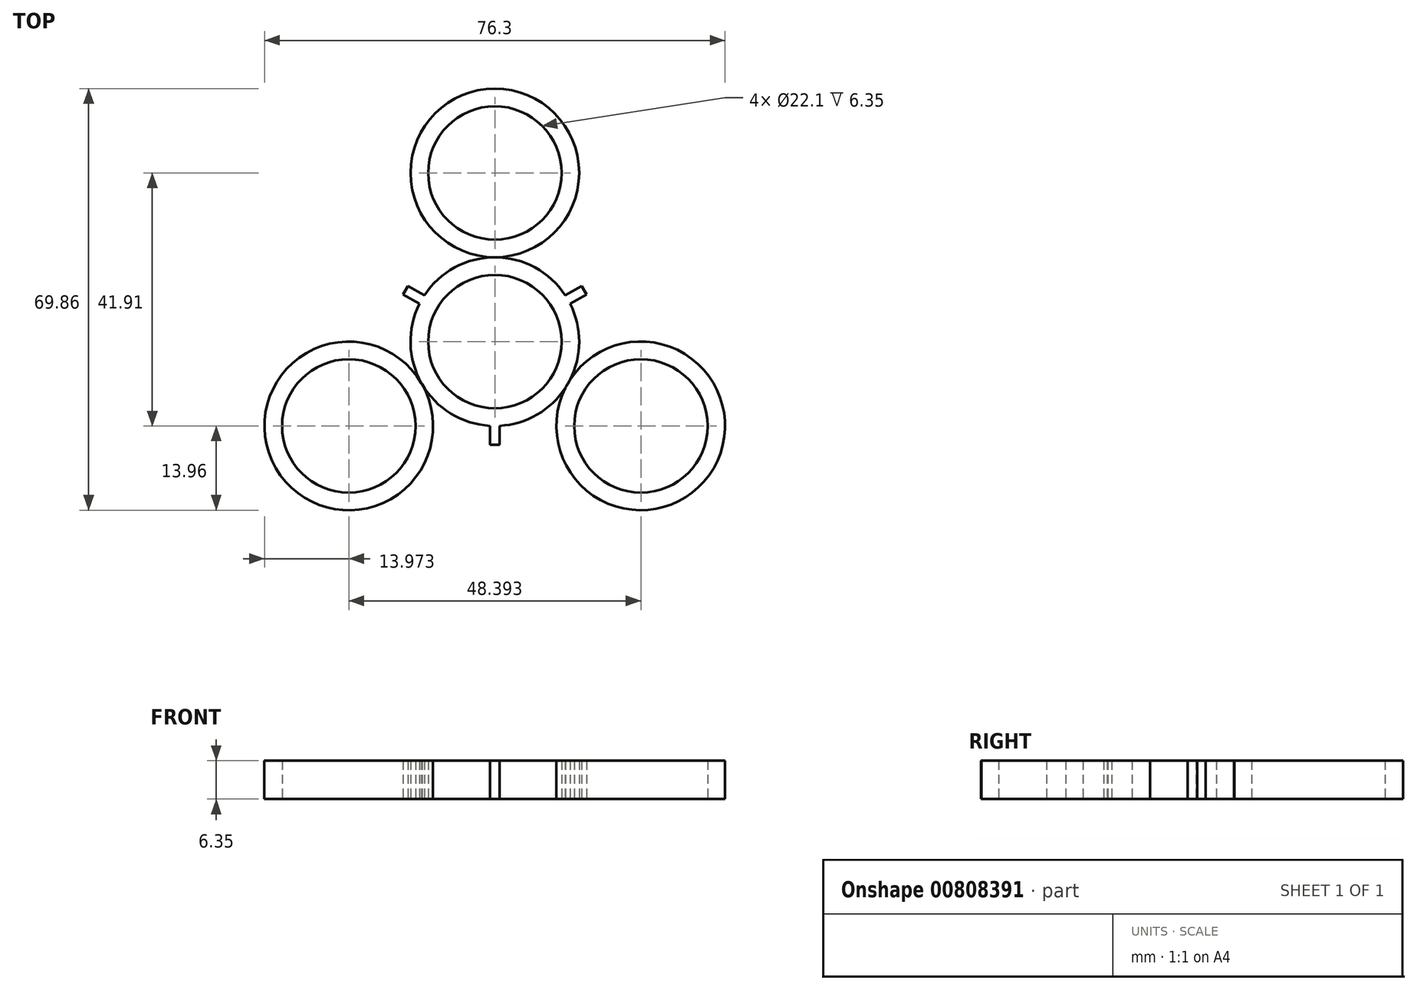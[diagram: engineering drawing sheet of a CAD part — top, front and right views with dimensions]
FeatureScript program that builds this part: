
annotation { "Feature Type Name" : "Feature", "Feature Type Description" : "" }
export const myFeature = defineFeature(function(context is Context, id is Id, definition is map)
    precondition{}
    {
        {
            var Q0;
            Q0=qCreatedBy(makeId("Top.planeOp"),FACE);
            var sketch = newSketch(context, id + "F0", { "sketchPlane" : qUnion([Q0])});
            skCircle(sketch, "E0", {"center": v(0, 0) * mm, "radius": 44.45 * mm});
            skCircle(sketch, "E1", {"center": v(0, 0) * mm, "radius": 11.05 * mm});
            skLineSegment(sketch, "E2", {"start": v(0, 0) * mm, "end": v(0, 27.94) * mm});
            skCircle(sketch, "E3", {"center": v(0, 27.94) * mm, "radius": 11.05 * mm});
            skCircle(sketch, "E4.1.0", {"center": v(-24.2, -13.97) * mm, "radius": 11.05 * mm});
            skCircle(sketch, "E4.2.0", {"center": v(24.2, -13.97) * mm, "radius": 11.05 * mm});
            skSolve(sketch);
        }
        {
            var Q0;
            Q0=makeQuery(id+"F0.imprint","IMPRINT",FACE,{"disambiguationData":[TD([[makeQuery(id+"F0.imprint","IMPRINT",EDGE,{"derivedFrom":sQuery(id+"F0.wireOp",EDGE,"E0")}),1.0]])]});
            var sketch = newSketch(context, id + "F1", { "sketchPlane" : qUnion([Q0])});
            skCircle(sketch, "E5", {"center": v(0, 27.96) * mm, "radius": 13.97 * mm});
            skCircle(sketch, "E6", {"center": v(24.16, -13.95) * mm, "radius": 13.97 * mm});
            skCircle(sketch, "E7", {"center": v(0, 0) * mm, "radius": 13.97 * mm});
            skCircle(sketch, "E8", {"center": v(-24.2, -13.96) * mm, "radius": 13.97 * mm});
            skSolve(sketch);
        }
        {
            var Q0;
            Q0=makeQuery(id+"F1.imprint","IMPRINT",FACE,{"disambiguationData":[TD([[makeQuery(id+"F1.imprint","IMPRINT",EDGE,{"derivedFrom":sQuery(id+"F1.wireOp",EDGE,"E5")}),1.0]])]});
            var Q1;
            Q1=makeQuery(id+"F1.imprint","IMPRINT",FACE,{"disambiguationData":[TD([[makeQuery(id+"F1.imprint","IMPRINT",EDGE,{"derivedFrom":makeQuery(id+"F0.imprint","IMPRINT",EDGE,{"derivedFrom":sQuery(id+"F0.wireOp",EDGE,"E1")})}),-1.0]])]});
            var Q2;
            Q2=makeQuery(id+"F1.imprint","IMPRINT",FACE,{"disambiguationData":[TD([[makeQuery(id+"F1.imprint","IMPRINT",EDGE,{"derivedFrom":makeQuery(id+"F0.imprint","IMPRINT",EDGE,{"derivedFrom":sQuery(id+"F0.wireOp",EDGE,"E4.1.0")})}),-1.0]])]});
            var Q3;
            Q3=makeQuery(id+"F1.imprint","IMPRINT",FACE,{"disambiguationData":[TD([[makeQuery(id+"F1.imprint","IMPRINT",EDGE,{"derivedFrom":makeQuery(id+"F0.imprint","IMPRINT",EDGE,{"derivedFrom":sQuery(id+"F0.wireOp",EDGE,"E4.2.0")})}),-1.0]])]});
            extrude(context, id + "F2", {"entities" : qUnion([Q0, Q1, Q2, Q3]), "depth" : 6.35 * mm, "offsetDistance" : 25.4 * mm});
        }
        {
            var Q0;
            Q0=qCreatedBy(makeId("Top.planeOp"),FACE);
            var sketch = newSketch(context, id + "F3", { "sketchPlane" : qUnion([Q0])});
            skArc(sketch, "E9", {"start": v(11.46, -19.74) * mm, "mid": v(-0.17, -17.05) * mm, "end": v(-11.76, -19.93) * mm});
            skArc(sketch, "E10.1.0", {"start": v(11.37, 19.8) * mm, "mid": v(14.85, 8.38) * mm, "end": v(23.14, -0.22) * mm});
            skArc(sketch, "E10.2.0", {"start": v(-22.83, -0.05) * mm, "mid": v(-14.68, 8.67) * mm, "end": v(-11.38, 20.15) * mm});
            skPoint(sketch, "E10.center", {"position": v(0, 0) * mm});
            skSolve(sketch);
        }
        {
            var Q0;
            Q0=sQuery(id+"F3.wireOp",EDGE,"E9");
            extrude(context, id + "F4", {"bodyType" : ToolBodyType.SURFACE, "surfaceEntities" : qUnion([Q0]), "depth" : 6.35 * mm, "offsetDistance" : 25.4 * mm});
        }
        {
            var Q0;
            Q0=sQuery(id+"F3.wireOp",EDGE,"E10.2.0");
            var Q1;
            Q1=sQuery(id+"F3.wireOp",EDGE,"E10.1.0");
            extrude(context, id + "F5", {"bodyType" : ToolBodyType.SURFACE, "surfaceEntities" : qUnion([Q0, Q1]), "depth" : 6.35 * mm, "offsetDistance" : 25.4 * mm});
        }
        {
            var Q0;
            Q0=qCreatedBy(makeId("Top.planeOp"),FACE);
            var sketch = newSketch(context, id + "F6", { "sketchPlane" : qUnion([Q0])});
            skLineSegment(sketch, "E11.bottom", {"start": v(0.8, -17.07) * mm, "end": v(-0.8, -17.07) * mm});
            skLineSegment(sketch, "E11.top", {"start": v(0.8, -13.9) * mm, "end": v(-0.8, -13.9) * mm});
            skLineSegment(sketch, "E11.left", {"start": v(0.8, -17.07) * mm, "end": v(0.8, -13.9) * mm});
            skLineSegment(sketch, "E11.right", {"start": v(-0.8, -17.07) * mm, "end": v(-0.8, -13.9) * mm});
            skPoint(sketch, "E11.middle", {"position": v(0, -15.49) * mm});
            skPoint(sketch, "E12.1.0", {"position": v(13.41, 7.74) * mm});
            skLineSegment(sketch, "E12.1.1", {"start": v(11.64, 7.65) * mm, "end": v(12.44, 6.25) * mm});
            skLineSegment(sketch, "E12.1.2", {"start": v(14.38, 9.23) * mm, "end": v(15.19, 7.84) * mm});
            skLineSegment(sketch, "E12.1.3", {"start": v(14.38, 9.23) * mm, "end": v(11.64, 7.65) * mm});
            skLineSegment(sketch, "E12.1.4", {"start": v(15.19, 7.84) * mm, "end": v(12.44, 6.25) * mm});
            skPoint(sketch, "E12.2.0", {"position": v(-13.41, 7.74) * mm});
            skLineSegment(sketch, "E12.2.1", {"start": v(-12.44, 6.25) * mm, "end": v(-11.64, 7.65) * mm});
            skLineSegment(sketch, "E12.2.2", {"start": v(-15.19, 7.84) * mm, "end": v(-14.38, 9.23) * mm});
            skLineSegment(sketch, "E12.2.3", {"start": v(-15.19, 7.84) * mm, "end": v(-12.44, 6.25) * mm});
            skLineSegment(sketch, "E12.2.4", {"start": v(-14.38, 9.23) * mm, "end": v(-11.64, 7.65) * mm});
            skPoint(sketch, "E12.center", {"position": v(0, 0) * mm});
            skSolve(sketch);
        }
        {
            var Q0;
            Q0 = qSketchRegion(id + "F6", true);
            extrude(context, id + "F7", {"entities" : qUnion([Q0]), "operationType" : NewBodyOperationType.ADD, "depth" : 6.35 * mm, "offsetDistance" : 25.4 * mm});
        }
    });
